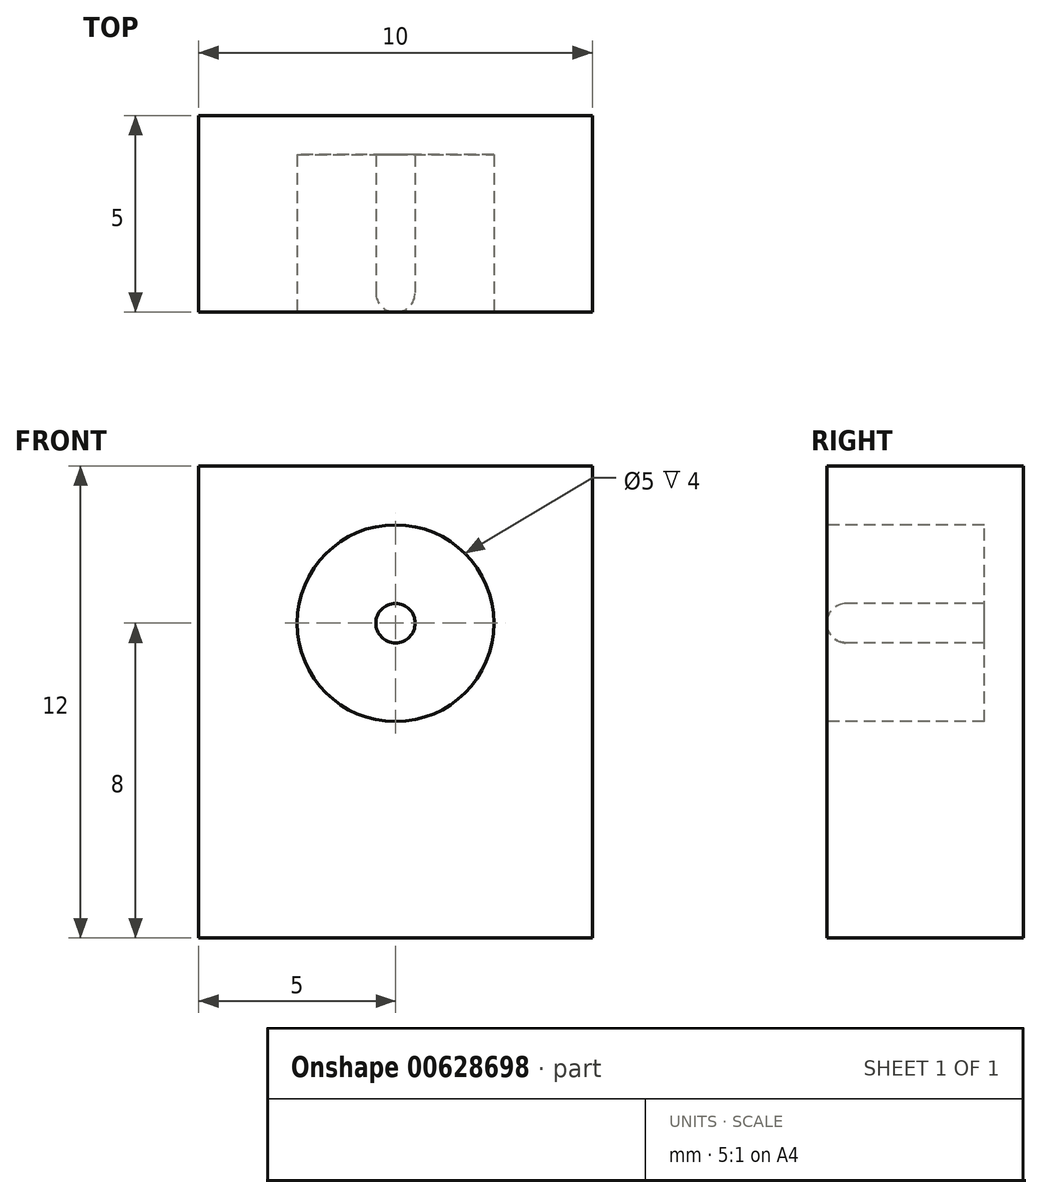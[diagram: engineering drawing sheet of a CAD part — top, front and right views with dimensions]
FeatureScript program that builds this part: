
annotation { "Feature Type Name" : "Feature", "Feature Type Description" : "" }
export const myFeature = defineFeature(function(context is Context, id is Id, definition is map)
    precondition{}
    {
        {
            var Q0;
            Q0=qCreatedBy(makeId("Front.planeOp"),FACE);
            var sketch = newSketch(context, id + "F0", { "sketchPlane" : qUnion([Q0])});
            skLineSegment(sketch, "E0.bottom", {"start": v(5, 6) * mm, "end": v(-5, 6) * mm});
            skLineSegment(sketch, "E0.top", {"start": v(5, -6) * mm, "end": v(-5, -6) * mm});
            skLineSegment(sketch, "E0.left", {"start": v(5, 6) * mm, "end": v(5, -6) * mm});
            skLineSegment(sketch, "E0.right", {"start": v(-5, 6) * mm, "end": v(-5, -6) * mm});
            skPoint(sketch, "E0.middle", {"position": v(0, 0) * mm});
            skSolve(sketch);
        }
        {
            var Q0;
            Q0 = qSketchRegion(id + "F0", true);
            extrude(context, id + "F1", {"entities" : qUnion([Q0]), "endBound" : BoundingType.SYMMETRIC, "depth" : 5 * mm, "offsetDistance" : 25 * mm});
        }
        {
            var Q0;
            Q0=makeQuery(id+"F1.opExtrude","CAP_FACE",FACE,{"disambiguationData":[OSD([sQuery(id+"F0.wireOp",EDGE,"E0.bottom"),sQuery(id+"F0.wireOp",EDGE,"E0.top"),sQuery(id+"F0.wireOp",EDGE,"E0.left"),sQuery(id+"F0.wireOp",EDGE,"E0.right")])],"isStart":false});
            var sketch = newSketch(context, id + "F2", { "sketchPlane" : qUnion([Q0])});
            skCircle(sketch, "E1", {"center": v(0, 2) * mm, "radius": 2.5 * mm});
            skCircle(sketch, "E2", {"center": v(0, 2) * mm, "radius": 0.5 * mm});
            skSolve(sketch);
        }
        {
            var Q0;
            Q0=makeQuery(id+"F2.imprint","IMPRINT",FACE,{"disambiguationData":[TD([[makeQuery(id+"F2.imprint","IMPRINT",EDGE,{"derivedFrom":sQuery(id+"F2.wireOp",EDGE,"E1")}),1.0]])]});
            extrude(context, id + "F3", {"entities" : qUnion([Q0]), "operationType" : NewBodyOperationType.REMOVE, "oppositeDirection" : true, "depth" : 4 * mm, "offsetDistance" : 25 * mm});
        }
        {
            var Q0;
            Q0=makeQuery(id+"F3.boolean.opBoolean","COPY",EDGE,{"derivedFrom":makeQuery(id+"F3.opExtrude","CAP_EDGE",EDGE,{"disambiguationData":[OSD([sQuery(id+"F2.wireOp",EDGE,"E2")])],"isStart":true})});
            fillet(context, id + "F4", {"entities" : qUnion([Q0]), "radius" : .5 * mm, "tangentPropagation" : true, "allowEdgeOverflow" : false});
        }
    });
